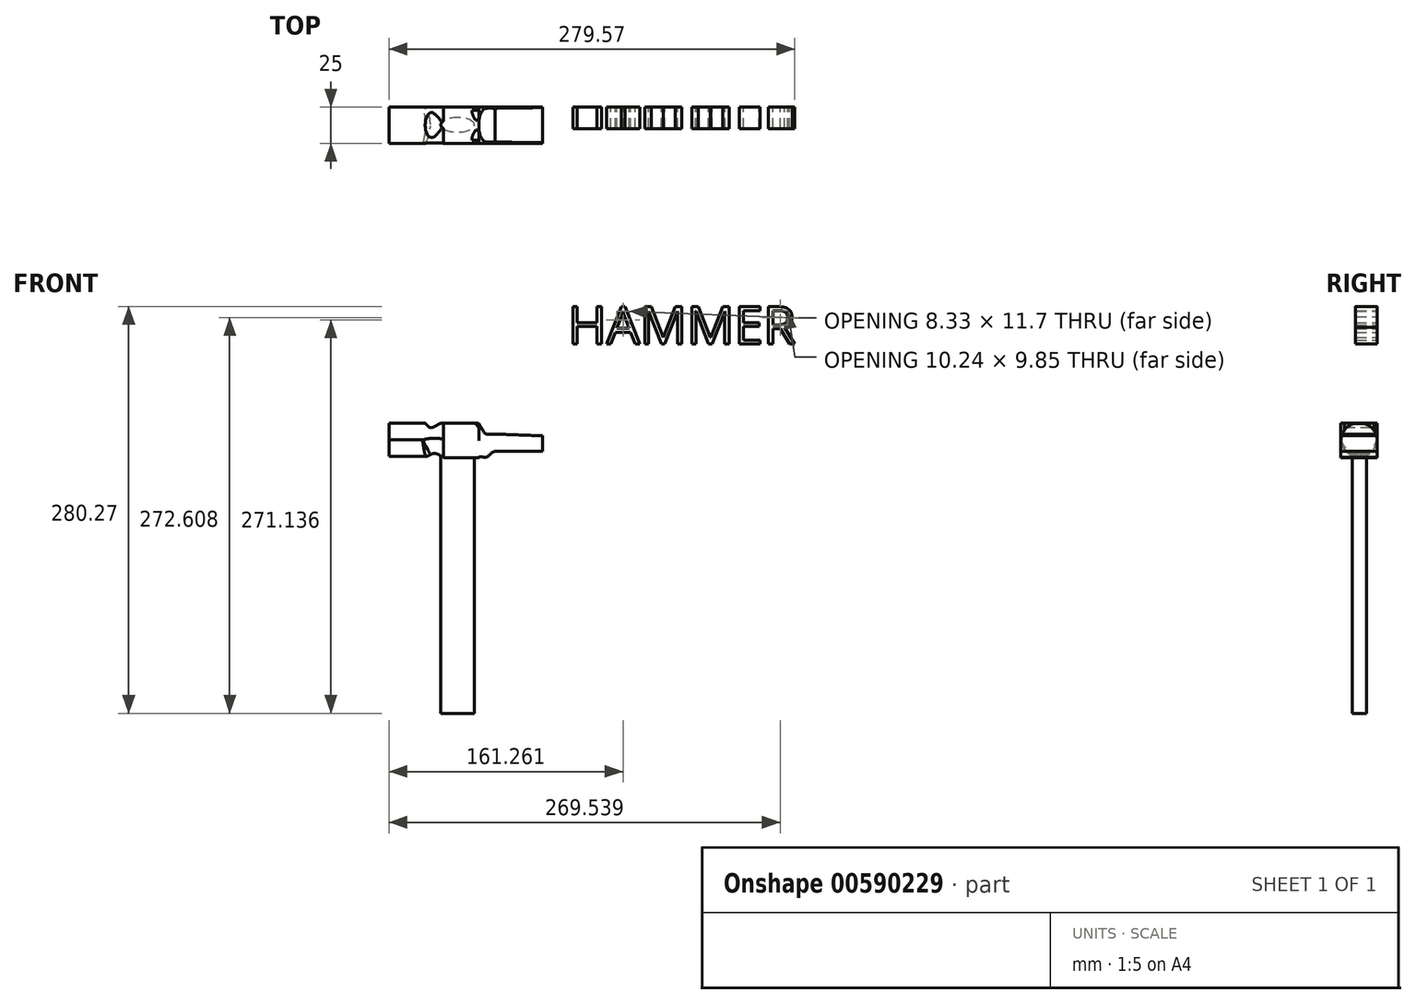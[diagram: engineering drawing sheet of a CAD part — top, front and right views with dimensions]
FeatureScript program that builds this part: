
annotation { "Feature Type Name" : "Feature", "Feature Type Description" : "" }
export const myFeature = defineFeature(function(context is Context, id is Id, definition is map)
    precondition{}
    {
        {
            var Q0;
            Q0=qCreatedBy(makeId("Front.planeOp"),FACE);
            var sketch = newSketch(context, id + "F0", { "sketchPlane" : qUnion([Q0])});
            skLineSegment(sketch, "E0.bottom", {"start": v(-37.4, 0) * mm, "end": v(-12.4, 0) * mm});
            skLineSegment(sketch, "E0.top", {"start": v(-37.4, -23.02) * mm, "end": v(-12.4, -23.02) * mm});
            skLineSegment(sketch, "E0.left", {"start": v(-37.4, 0) * mm, "end": v(-37.4, -23.02) * mm});
            skLineSegment(sketch, "E0.right", {"start": v(-12.4, 0) * mm, "end": v(-12.4, -23.02) * mm});
            skLineSegment(sketch, "E1.bottom", {"start": v(0, 0) * mm, "end": v(24.42, 0) * mm});
            skLineSegment(sketch, "E1.top", {"start": v(0, -23.6) * mm, "end": v(24.42, -23.6) * mm});
            skLineSegment(sketch, "E1.left", {"start": v(0, 0) * mm, "end": v(0, -23.6) * mm});
            skLineSegment(sketch, "E1.right", {"start": v(24.42, 0) * mm, "end": v(24.42, -23.6) * mm});
            skLineSegment(sketch, "E2", {"start": v(35.67, -7.55) * mm, "end": v(35.67, -19.4) * mm});
            skLineSegment(sketch, "E3", {"start": v(35.67, -19.4) * mm, "end": v(68.45, -19.4) * mm});
            skLineSegment(sketch, "E4", {"start": v(68.45, -19.4) * mm, "end": v(68.45, -8.8) * mm});
            skLineSegment(sketch, "E5", {"start": v(68.45, -8.8) * mm, "end": v(35.67, -7.55) * mm});
            skFitSpline(sketch, "E6", {"points": [v(-12.4, 0) * mm, v(-8, -3.15) * mm, v(0, 0) * mm], "startDerivative": vector(8.48, -9.9) * mm, "endDerivative": vector(18.08, 0) * mm});
            skFitSpline(sketch, "E7", {"points": [v(-12.4, -23.02) * mm, v(-6.7, -20.88) * mm, v(0, -23.6) * mm], "startDerivative": vector(13.96, 0) * mm, "endDerivative": vector(12.65, -7.92) * mm});
            skFitSpline(sketch, "E8", {"points": [v(24.42, 0) * mm, v(29.42, -7.31) * mm, v(35.67, -7.55) * mm], "startDerivative": vector(8.47, -14.5) * mm, "endDerivative": vector(14.14, -0.3) * mm});
            skFitSpline(sketch, "E9", {"points": [v(24.42, -23.6) * mm, v(29.46, -23.6) * mm, v(35.67, -19.4) * mm], "startDerivative": vector(9.66, 7.78) * mm, "endDerivative": vector(12.82, 0.53) * mm});
            skSolve(sketch);
        }
        {
            var Q0;
            Q0 = qSketchRegion(id + "F0", true);
            extrude(context, id + "F1", {"entities" : qUnion([Q0]), "depth" : 25 * mm, "offsetDistance" : 25 * mm});
        }
        {
            var Q0;
            Q0=makeQuery(id+"F1.opExtrude","CAP_EDGE",EDGE,{"disambiguationData":[OSD([sQuery(id+"F0.wireOp",EDGE,"E0.bottom")])],"isStart":false});
            var Q1;
            Q1=makeQuery(id+"F1.opExtrude","CAP_EDGE",EDGE,{"disambiguationData":[OSD([sQuery(id+"F0.wireOp",EDGE,"E0.bottom")])],"isStart":true});
            var Q2;
            Q2=makeQuery(id+"F1.opExtrude","CAP_EDGE",EDGE,{"disambiguationData":[OSD([sQuery(id+"F0.wireOp",EDGE,"E0.top")])],"isStart":false});
            var Q3;
            Q3=makeQuery(id+"F1.opExtrude","CAP_EDGE",EDGE,{"disambiguationData":[OSD([sQuery(id+"F0.wireOp",EDGE,"E0.top")])],"isStart":true});
            fillet(context, id + "F2", {"entities" : qUnion([Q0, Q1, Q2, Q3]), "radius" : 12 * mm, "tangentPropagation" : true, "allowEdgeOverflow" : false});
        }
        {
            var Q0;
            Q0=qCreatedBy(makeId("Front.planeOp"),FACE);
            var sketch = newSketch(context, id + "F3", { "sketchPlane" : qUnion([Q0])});
            skLineSegment(sketch, "E10.bottom", {"start": v(0, 0) * mm, "end": v(24.72, 0) * mm});
            skLineSegment(sketch, "E10.top", {"start": v(0, -23.83) * mm, "end": v(24.72, -23.83) * mm});
            skLineSegment(sketch, "E10.left", {"start": v(0, 0) * mm, "end": v(0, -23.83) * mm});
            skLineSegment(sketch, "E10.right", {"start": v(24.72, 0) * mm, "end": v(24.72, -23.83) * mm});
            skSolve(sketch);
        }
        {
            var Q0;
            Q0 = qSketchRegion(id + "F3", true);
            extrude(context, id + "F4", {"entities" : qUnion([Q0]), "operationType" : NewBodyOperationType.ADD, "depth" : 25 * mm, "offsetDistance" : 25 * mm});
        }
        {
            var Q0;
            Q0=makeQuery(id+"F4.opExtrude","SWEPT_EDGE",EDGE,{"disambiguationData":[OSD([sQuery(id+"F3.wireOp",EDGE,"E10.bottom"),sQuery(id+"F3.wireOp",EDGE,"E10.right")])]});
            fillet(context, id + "F5", {"entities" : qUnion([Q0]), "radius" : 5 * mm, "tangentPropagation" : true, "allowEdgeOverflow" : false});
        }
        {
            var Q0;
            Q0=qCreatedBy(makeId("Top.planeOp"),FACE);
            var sketch = newSketch(context, id + "F6", { "sketchPlane" : qUnion([Q0])});
            skEllipse(sketch, "E11", {"center": v(9.92, -12.29) * mm, "majorRadius": 11.55 * mm, "minorRadius": 5.01 * mm, "majorAxis": v(1, 0)});
            skSolve(sketch);
        }
        {
            var Q0;
            Q0 = qSketchRegion(id + "F6", true);
            extrude(context, id + "F7", {"entities" : qUnion([Q0]), "operationType" : NewBodyOperationType.ADD, "depth" : -200 * mm, "offsetDistance" : 25 * mm});
        }
        {
            var Q0;
            Q0=qCreatedBy(makeId("Front.planeOp"),FACE);
            var sketch = newSketch(context, id + "F8", { "sketchPlane" : qUnion([Q0])});
            skText(sketch, "E12", { "text": "HAMMER", "fontName": "OpenSans-Regular.ttf"});
            const initialGuessF8  = {"E12": [0.0858, 0.0544, 1, 0, 0.02598]};
            skSetInitialGuess(sketch, initialGuessF8);
            skSolve(sketch);
        }
        {
            var Q0;
            Q0 = qSketchRegion(id + "F8", true);
            extrude(context, id + "F9", {"entities" : qUnion([Q0]), "depth" : 15 * mm, "offsetDistance" : 25 * mm});
        }
    });
